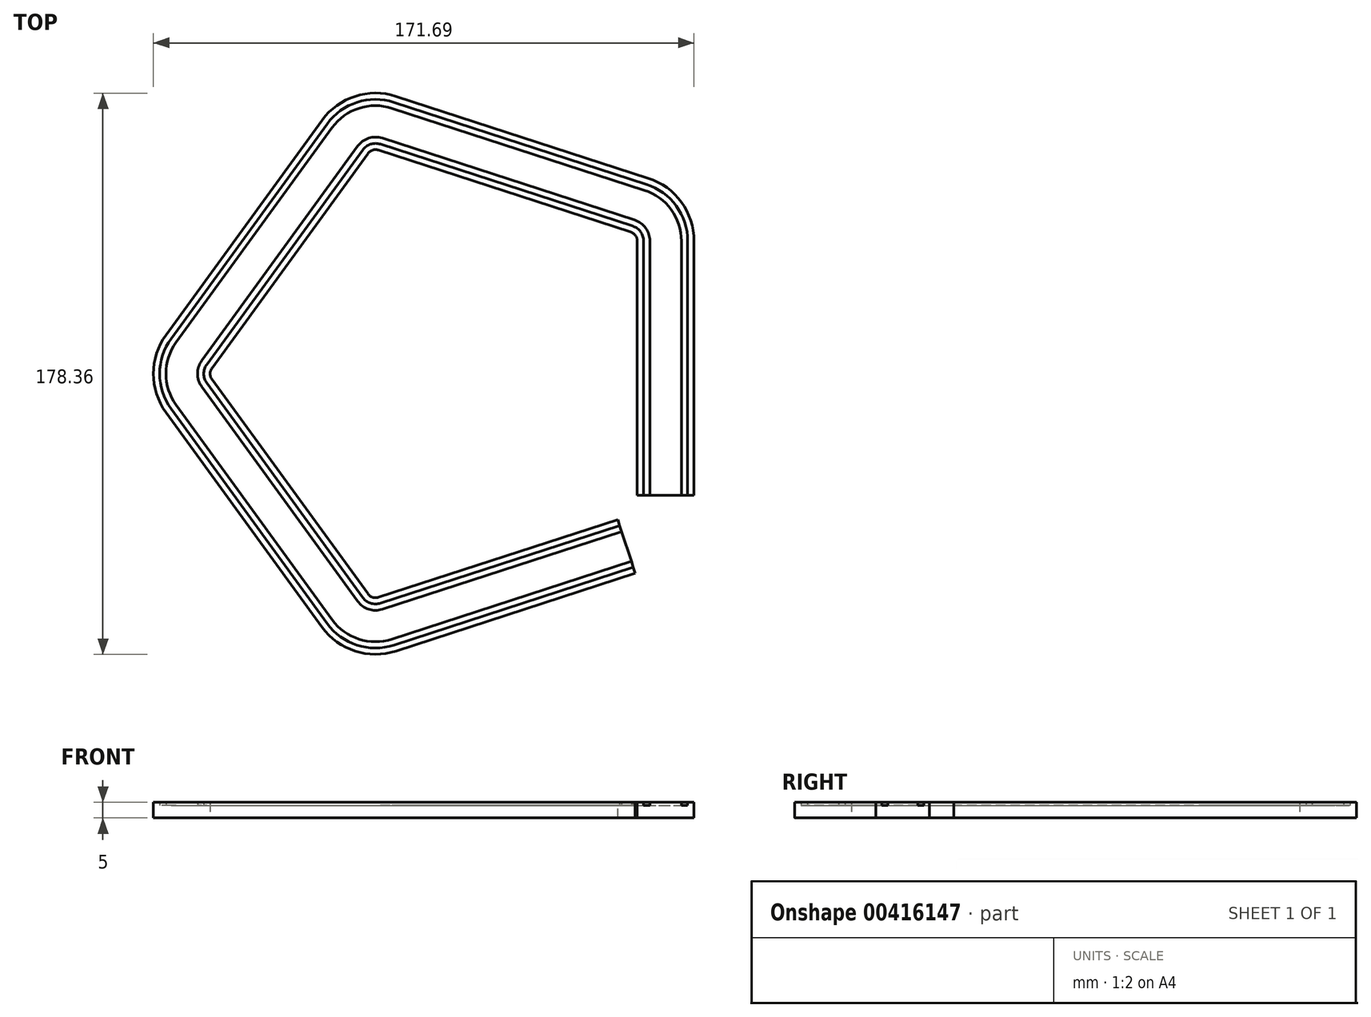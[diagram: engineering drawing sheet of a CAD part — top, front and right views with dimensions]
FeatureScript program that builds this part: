
annotation { "Feature Type Name" : "Feature", "Feature Type Description" : "" }
export const myFeature = defineFeature(function(context is Context, id is Id, definition is map)
    precondition{}
    {
        {
            var Q0;
            Q0=qCreatedBy(makeId("Top.planeOp"),FACE);
            var sketch = newSketch(context, id + "F0", { "sketchPlane" : qUnion([Q0])});
            skCircle(sketch, "E0.cCircle", {"center": v(0, 0) * mm, "radius": 70 * mm, "construction": true});
            skLineSegment(sketch, "E0.0", {"start": v(70, 42.14) * mm, "end": v(70, -38.67) * mm});
            skLineSegment(sketch, "E0.1", {"start": v(57.56, -54.9) * mm, "end": v(-18.45, -79.6) * mm});
            skLineSegment(sketch, "E0.2", {"start": v(-31.86, -75.24) * mm, "end": v(-81.4, -7.05) * mm});
            skLineSegment(sketch, "E0.3", {"start": v(-81.4, 7.05) * mm, "end": v(-31.86, 75.24) * mm});
            skLineSegment(sketch, "E0.4", {"start": v(-18.45, 79.6) * mm, "end": v(61.7, 53.55) * mm});
            skPoint(sketch, "E0.0.midPoint", {"position": v(70, 0) * mm});
            skPoint(sketch, "E1.visualSharp", {"position": v(-26.74, 82.29) * mm});
            skArc(sketch, "E1.filletArc", {"start": v(-18.45, 79.6) * mm, "mid": v(-25.86, 79.6) * mm, "end": v(-31.86, 75.24) * mm});
            skPoint(sketch, "E2.visualSharp", {"position": v(70, 50.86) * mm});
            skArc(sketch, "E2.filletArc", {"start": v(70, 42.14) * mm, "mid": v(67.7, 49.2) * mm, "end": v(61.7, 53.55) * mm});
            skPoint(sketch, "E3.visualSharp", {"position": v(70, -50.86) * mm});
            skPoint(sketch, "E4.visualSharp", {"position": v(-26.74, -82.29) * mm});
            skArc(sketch, "E4.filletArc", {"start": v(-31.86, -75.24) * mm, "mid": v(-25.86, -79.6) * mm, "end": v(-18.45, -79.6) * mm});
            skPoint(sketch, "E5.visualSharp", {"position": v(-86.52, 0) * mm});
            skArc(sketch, "E5.filletArc", {"start": v(-81.4, 7.05) * mm, "mid": v(-83.7, 0) * mm, "end": v(-81.4, -7.05) * mm});
            skSolve(sketch);
        }
        {
            var Q0;
            Q0=qCreatedBy(makeId("Front.planeOp"),FACE);
            var sketch = newSketch(context, id + "F1", { "sketchPlane" : qUnion([Q0])});
            skLineSegment(sketch, "E6.bottom", {"start": v(79, -2.5) * mm, "end": v(61, -2.5) * mm});
            skLineSegment(sketch, "E6.top", {"start": v(79, 2.5) * mm, "end": v(77, 2.5) * mm});
            skLineSegment(sketch, "E6.left", {"start": v(79, -2.5) * mm, "end": v(79, 2.5) * mm});
            skLineSegment(sketch, "E6.right", {"start": v(61, -2.5) * mm, "end": v(61, 2.5) * mm});
            skPoint(sketch, "E6.middle", {"position": v(70, 0) * mm});
            skLineSegment(sketch, "E7.top", {"start": v(63, 1.5) * mm, "end": v(65, 1.5) * mm});
            skLineSegment(sketch, "E7.left", {"start": v(63, 2.5) * mm, "end": v(63, 1.5) * mm});
            skLineSegment(sketch, "E7.right", {"start": v(65, 2.5) * mm, "end": v(65, 1.5) * mm});
            skLineSegment(sketch, "E8", {"start": v(70, 2.5) * mm, "end": v(70, -2.1) * mm, "construction": true});
            skLineSegment(sketch, "E9", {"start": v(70, -2.1) * mm, "end": v(70, -2.5) * mm, "construction": true});
            skLineSegment(sketch, "E10.MirrorCS", {"start": v(77, 1.5) * mm, "end": v(75, 1.5) * mm});
            skLineSegment(sketch, "E11.MirrorCS", {"start": v(75, 2.5) * mm, "end": v(75, 1.5) * mm});
            skLineSegment(sketch, "E12.MirrorCS", {"start": v(77, 2.5) * mm, "end": v(77, 1.5) * mm});
            skLineSegment(sketch, "E13.trimOffspring", {"start": v(75, 2.5) * mm, "end": v(65, 2.5) * mm});
            skLineSegment(sketch, "E14.trimOffspring", {"start": v(63, 2.5) * mm, "end": v(61, 2.5) * mm});
            skSolve(sketch);
        }
        {
            var Q0;
            Q0=makeQuery(id+"F1.imprint","IMPRINT",FACE,{"disambiguationData":[TD([[makeQuery(id+"F1.imprint","IMPRINT",EDGE,{"derivedFrom":sQuery(id+"F1.wireOp",EDGE,"E6.bottom")}),-1.0]])]});
            var Q1;
            Q1=qConstructionFilter(qBodyType(qCreatedBy(id+"F0",EDGE),BodyType.WIRE),ConstructionObject.NO);
            sweep(context, id + "F2", {"profiles" : qUnion([Q0]), "path" : qUnion([Q1])});
        }
    });
